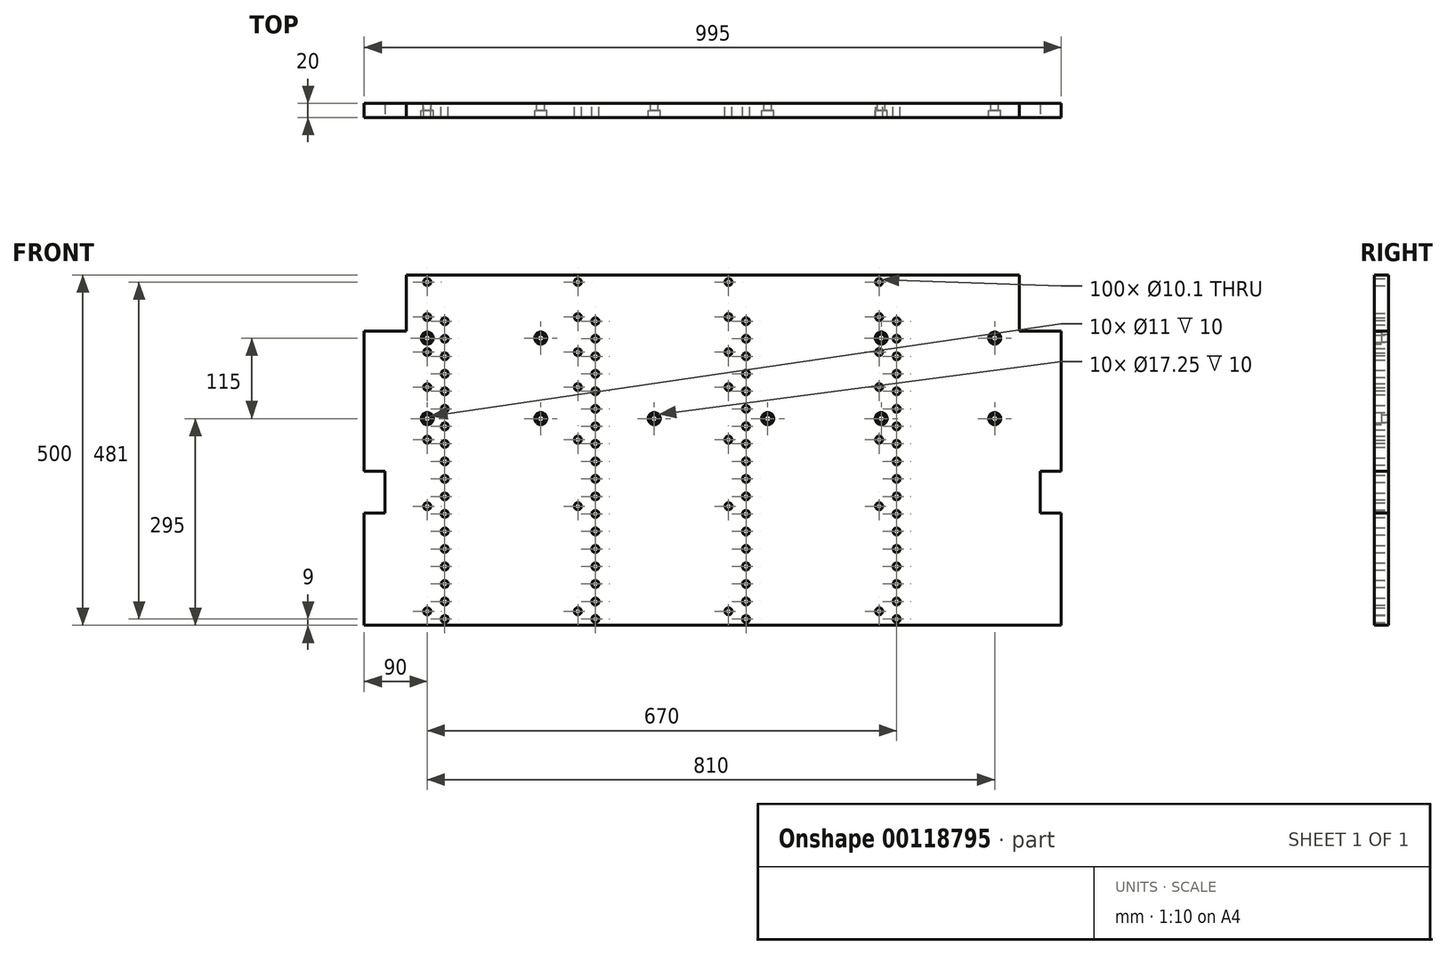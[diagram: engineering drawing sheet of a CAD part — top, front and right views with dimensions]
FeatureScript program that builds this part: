
annotation { "Feature Type Name" : "Feature", "Feature Type Description" : "" }
export const myFeature = defineFeature(function(context is Context, id is Id, definition is map)
    precondition{}
    {
        {
            var Q0;
            Q0=qCreatedBy(makeId("Front.planeOp"),FACE);
            var sketch = newSketch(context, id + "F0", { "sketchPlane" : qUnion([Q0])});
            skLineSegment(sketch, "E0.bottom", {"start": v(497.5, -250) * mm, "end": v(-497.5, -250) * mm});
            skLineSegment(sketch, "E0.top", {"start": v(437.5, 250) * mm, "end": v(-437.5, 250) * mm});
            skLineSegment(sketch, "E0.left", {"start": v(497.5, -250) * mm, "end": v(497.5, -90) * mm});
            skLineSegment(sketch, "E0.right", {"start": v(-497.5, -250) * mm, "end": v(-497.5, -90) * mm});
            skPoint(sketch, "E0.middle", {"position": v(0, 0) * mm});
            skLineSegment(sketch, "E1", {"start": v(-497.5, 170) * mm, "end": v(-437.5, 170) * mm});
            skLineSegment(sketch, "E2", {"start": v(-437.5, 170) * mm, "end": v(-437.5, 250) * mm});
            skLineSegment(sketch, "E3.MirrorCS", {"start": v(437.5, 170) * mm, "end": v(437.5, 250) * mm});
            skLineSegment(sketch, "E4.MirrorCS", {"start": v(497.5, 170) * mm, "end": v(437.5, 170) * mm});
            skLineSegment(sketch, "E5", {"start": v(-497.5, -30) * mm, "end": v(-467.5, -30) * mm});
            skLineSegment(sketch, "E6", {"start": v(-467.5, -30) * mm, "end": v(-467.5, -90) * mm});
            skLineSegment(sketch, "E7", {"start": v(-467.5, -90) * mm, "end": v(-497.5, -90) * mm});
            skLineSegment(sketch, "E8.MirrorCS", {"start": v(467.5, -30) * mm, "end": v(467.5, -90) * mm});
            skLineSegment(sketch, "E9.MirrorCS", {"start": v(467.5, -90) * mm, "end": v(497.5, -90) * mm});
            skLineSegment(sketch, "E10.MirrorCS", {"start": v(497.5, -30) * mm, "end": v(467.5, -30) * mm});
            skLineSegment(sketch, "E11.trimOffspring", {"start": v(-497.5, -30) * mm, "end": v(-497.5, 170) * mm});
            skLineSegment(sketch, "E12.trimOffspring", {"start": v(497.5, -30) * mm, "end": v(497.5, 170) * mm});
            skPoint(sketch, "E13.orphan", {"position": v(-497.5, 250) * mm});
            skPoint(sketch, "E14.orphan", {"position": v(497.5, 250) * mm});
            skSolve(sketch);
        }
        {
            var Q0;
            Q0=makeQuery(id+"F0.imprint","IMPRINT",FACE,{"disambiguationData":[TD([[makeQuery(id+"F0.imprint","IMPRINT",EDGE,{"derivedFrom":sQuery(id+"F0.wireOp",EDGE,"E0.bottom")}),-1.0]])]});
            extrude(context, id + "F1", {"entities" : qUnion([Q0]), "oppositeDirection" : true, "depth" : 20 * mm, "offsetDistance" : 25 * mm});
        }
        {
            var Q0;
            Q0=makeQuery(id+"F1.opExtrude","CAP_FACE",FACE,{"disambiguationData":[OSD([sQuery(id+"F0.wireOp",EDGE,"E0.bottom"),sQuery(id+"F0.wireOp",EDGE,"E0.top"),sQuery(id+"F0.wireOp",EDGE,"E0.left"),sQuery(id+"F0.wireOp",EDGE,"E0.right"),sQuery(id+"F0.wireOp",EDGE,"E1"),sQuery(id+"F0.wireOp",EDGE,"E2"),sQuery(id+"F0.wireOp",EDGE,"E3.MirrorCS"),sQuery(id+"F0.wireOp",EDGE,"E4.MirrorCS"),sQuery(id+"F0.wireOp",EDGE,"E5"),sQuery(id+"F0.wireOp",EDGE,"E6"),sQuery(id+"F0.wireOp",EDGE,"E7"),sQuery(id+"F0.wireOp",EDGE,"E8.MirrorCS"),sQuery(id+"F0.wireOp",EDGE,"E9.MirrorCS"),sQuery(id+"F0.wireOp",EDGE,"E10.MirrorCS"),sQuery(id+"F0.wireOp",EDGE,"E11.trimOffspring"),sQuery(id+"F0.wireOp",EDGE,"E12.trimOffspring")])],"isStart":true});
            var sketch = newSketch(context, id + "F2", { "sketchPlane" : qUnion([Q0])});
            skPoint(sketch, "E15", {"position": v(-407.5, 160) * mm});
            skPoint(sketch, "E16.0.1.0", {"position": v(-407.5, 45) * mm});
            skPoint(sketch, "E16.1.0.0", {"position": v(-245.5, 160) * mm});
            skPoint(sketch, "E16.1.1.0", {"position": v(-245.5, 45) * mm});
            skPoint(sketch, "E16.2.1.0", {"position": v(-83.5, 45) * mm});
            skPoint(sketch, "E16.3.1.0", {"position": v(78.5, 45) * mm});
            skPoint(sketch, "E16.4.0.0", {"position": v(240.5, 160) * mm});
            skPoint(sketch, "E16.4.1.0", {"position": v(240.5, 45) * mm});
            skPoint(sketch, "E16.5.0.0", {"position": v(402.5, 160) * mm});
            skPoint(sketch, "E16.5.1.0", {"position": v(402.5, 45) * mm});
            skLineSegment(sketch, "E16.direction1", {"start": v(-407.5, 160) * mm, "end": v(-245.5, 160) * mm, "construction": true});
            skLineSegment(sketch, "E16.direction2", {"start": v(-407.5, 160) * mm, "end": v(-407.5, 45) * mm, "construction": true});
            skSolve(sketch);
        }
        {
            var Q0;
            Q0=sQuery(id+"F2.wireOp",VERTEX,"E16.2.0.0");
            var Q1;
            Q1=sQuery(id+"F2.wireOp",VERTEX,"E16.2.1.0");
            var Q2;
            Q2=sQuery(id+"F2.wireOp",VERTEX,"E16.3.0.0");
            var Q3;
            Q3=sQuery(id+"F2.wireOp",VERTEX,"E15");
            var Q4;
            Q4=sQuery(id+"F2.wireOp",VERTEX,"E16.3.1.0");
            var Q5;
            Q5=sQuery(id+"F2.wireOp",VERTEX,"E16.0.1.0");
            var Q6;
            Q6=sQuery(id+"F2.wireOp",VERTEX,"E16.4.0.0");
            var Q7;
            Q7=sQuery(id+"F2.wireOp",VERTEX,"E16.1.0.0");
            var Q8;
            Q8=sQuery(id+"F2.wireOp",VERTEX,"E16.5.1.0");
            var Q9;
            Q9=sQuery(id+"F2.wireOp",VERTEX,"E16.4.1.0");
            var Q10;
            Q10=sQuery(id+"F2.wireOp",VERTEX,"E16.1.1.0");
            var Q11;
            Q11=sQuery(id+"F2.wireOp",VERTEX,"E16.5.0.0");
            var Q12;
            Q12=makeQuery(id+"F1.opExtrude","SWEPT_BODY",BODY,{"disambiguationData":[OSD([sQuery(id+"F0.wireOp",EDGE,"E0.bottom"),sQuery(id+"F0.wireOp",EDGE,"E0.top"),sQuery(id+"F0.wireOp",EDGE,"E0.left"),sQuery(id+"F0.wireOp",EDGE,"E0.right"),sQuery(id+"F0.wireOp",EDGE,"E1"),sQuery(id+"F0.wireOp",EDGE,"E2"),sQuery(id+"F0.wireOp",EDGE,"E3.MirrorCS"),sQuery(id+"F0.wireOp",EDGE,"E4.MirrorCS"),sQuery(id+"F0.wireOp",EDGE,"E5"),sQuery(id+"F0.wireOp",EDGE,"E6"),sQuery(id+"F0.wireOp",EDGE,"E7"),sQuery(id+"F0.wireOp",EDGE,"E8.MirrorCS"),sQuery(id+"F0.wireOp",EDGE,"E9.MirrorCS"),sQuery(id+"F0.wireOp",EDGE,"E10.MirrorCS"),sQuery(id+"F0.wireOp",EDGE,"E11.trimOffspring"),sQuery(id+"F0.wireOp",EDGE,"E12.trimOffspring")])]});
            hole(context, id + "F3", {"style" : HoleStyle.C_BORE, "endStyle" : HoleEndStyle.BLIND, "standardTappedOrClearance" : lookupTablePath({ "fit" : "Normal", "standard" : "ISO", "size" : "M10", "type" : "Clearance" }), "standardBlindInLast" : lookupTablePath({ "fit" : "Normal", "standard" : "ISO", "engagement" : "75%", "pitch" : "1 mm", "size" : "M10", "type" : "Clearance & tapped" }), "holeDiameter" : 11 * mm, "cBoreDiameter" : 17.25 * mm, "cBoreDepth" : 10 * mm, "majorDiameter" : 10 * mm, "holeDepth" : 35 * mm, "tappedDepth" : 32 * mm, "tapClearance" : 3, "locations" : qUnion([Q0, Q1, Q2, Q3, Q4, Q5, Q6, Q7, Q8, Q9, Q10, Q11]), "scope" : qUnion([Q12]), "startStyle" : HoleStartStyle.SKETCH});
        }
        {
            var Q0;
            Q0=makeQuery(id+"F1.opExtrude","CAP_FACE",FACE,{"disambiguationData":[OSD([sQuery(id+"F0.wireOp",EDGE,"E0.bottom"),sQuery(id+"F0.wireOp",EDGE,"E0.top"),sQuery(id+"F0.wireOp",EDGE,"E0.left"),sQuery(id+"F0.wireOp",EDGE,"E0.right"),sQuery(id+"F0.wireOp",EDGE,"E1"),sQuery(id+"F0.wireOp",EDGE,"E2"),sQuery(id+"F0.wireOp",EDGE,"E3.MirrorCS"),sQuery(id+"F0.wireOp",EDGE,"E4.MirrorCS"),sQuery(id+"F0.wireOp",EDGE,"E5"),sQuery(id+"F0.wireOp",EDGE,"E6"),sQuery(id+"F0.wireOp",EDGE,"E7"),sQuery(id+"F0.wireOp",EDGE,"E8.MirrorCS"),sQuery(id+"F0.wireOp",EDGE,"E9.MirrorCS"),sQuery(id+"F0.wireOp",EDGE,"E10.MirrorCS"),sQuery(id+"F0.wireOp",EDGE,"E11.trimOffspring"),sQuery(id+"F0.wireOp",EDGE,"E12.trimOffspring")])],"isStart":true});
            var sketch = newSketch(context, id + "F4", { "sketchPlane" : qUnion([Q0])});
            skLineSegment(sketch, "E17", {"start": v(-407.5, 250) * mm, "end": v(-407.5, -250) * mm, "construction": true});
            skPoint(sketch, "E18", {"position": v(-407.5, 240) * mm});
            skPoint(sketch, "E19", {"position": v(-407.5, 190) * mm});
            skPoint(sketch, "E20", {"position": v(-407.5, 140) * mm});
            skPoint(sketch, "E21", {"position": v(-407.5, 90) * mm});
            skPoint(sketch, "E22", {"position": v(-407.5, 15) * mm});
            skPoint(sketch, "E23", {"position": v(-407.5, -80) * mm});
            skPoint(sketch, "E24", {"position": v(-407.5, -230) * mm});
            skLineSegment(sketch, "E25.direction1", {"start": v(-407.5, -250) * mm, "end": v(-197.5, -250) * mm, "construction": true});
            skPoint(sketch, "E26.1.0.0", {"position": v(-192.5, 240) * mm});
            skPoint(sketch, "E26.1.0.1", {"position": v(-192.5, 190) * mm});
            skPoint(sketch, "E26.1.0.2", {"position": v(-192.5, 140) * mm});
            skPoint(sketch, "E26.1.0.3", {"position": v(-192.5, 90) * mm});
            skPoint(sketch, "E26.1.0.4", {"position": v(-192.5, 15) * mm});
            skPoint(sketch, "E26.1.0.5", {"position": v(-192.5, -80) * mm});
            skPoint(sketch, "E26.1.0.6", {"position": v(-192.5, -230) * mm});
            skLineSegment(sketch, "E26.1.0.7", {"start": v(-192.5, 250) * mm, "end": v(-192.5, -250) * mm, "construction": true});
            skPoint(sketch, "E26.2.0.0", {"position": v(22.5, 240) * mm});
            skPoint(sketch, "E26.2.0.1", {"position": v(22.5, 190) * mm});
            skPoint(sketch, "E26.2.0.2", {"position": v(22.5, 140) * mm});
            skPoint(sketch, "E26.2.0.3", {"position": v(22.5, 90) * mm});
            skPoint(sketch, "E26.2.0.4", {"position": v(22.5, 15) * mm});
            skPoint(sketch, "E26.2.0.5", {"position": v(22.5, -80) * mm});
            skPoint(sketch, "E26.2.0.6", {"position": v(22.5, -230) * mm});
            skLineSegment(sketch, "E26.2.0.7", {"start": v(22.5, 250) * mm, "end": v(22.5, -250) * mm, "construction": true});
            skPoint(sketch, "E26.3.0.0", {"position": v(237.5, 240) * mm});
            skPoint(sketch, "E26.3.0.1", {"position": v(237.5, 190) * mm});
            skPoint(sketch, "E26.3.0.2", {"position": v(237.5, 140) * mm});
            skPoint(sketch, "E26.3.0.3", {"position": v(237.5, 90) * mm});
            skPoint(sketch, "E26.3.0.4", {"position": v(237.5, 15) * mm});
            skPoint(sketch, "E26.3.0.5", {"position": v(237.5, -80) * mm});
            skPoint(sketch, "E26.3.0.6", {"position": v(237.5, -230) * mm});
            skLineSegment(sketch, "E26.3.0.7", {"start": v(237.5, 250) * mm, "end": v(237.5, -250) * mm, "construction": true});
            skPoint(sketch, "E26.4.0.0", {"position": v(452.5, 240) * mm});
            skPoint(sketch, "E26.4.0.1", {"position": v(452.5, 190) * mm});
            skPoint(sketch, "E26.4.0.2", {"position": v(452.5, 140) * mm});
            skPoint(sketch, "E26.4.0.3", {"position": v(452.5, 90) * mm});
            skPoint(sketch, "E26.4.0.4", {"position": v(452.5, 15) * mm});
            skPoint(sketch, "E26.4.0.5", {"position": v(452.5, -80) * mm});
            skPoint(sketch, "E26.4.0.6", {"position": v(452.5, -230) * mm});
            skLineSegment(sketch, "E26.4.0.7", {"start": v(452.5, 250) * mm, "end": v(452.5, -250) * mm, "construction": true});
            skLineSegment(sketch, "E26.direction1", {"start": v(-407.5, 190) * mm, "end": v(-192.5, 190) * mm, "construction": true});
            skSolve(sketch);
        }
        {
            var Q0;
            Q0=sQuery(id+"F4.wireOp",VERTEX,"E23");
            var Q1;
            Q1=sQuery(id+"F4.wireOp",VERTEX,"E22");
            var Q2;
            Q2=sQuery(id+"F4.wireOp",VERTEX,"E24");
            var Q3;
            Q3=sQuery(id+"F4.wireOp",VERTEX,"E21");
            var Q4;
            Q4=sQuery(id+"F4.wireOp",VERTEX,"E18");
            var Q5;
            Q5=sQuery(id+"F4.wireOp",VERTEX,"E20");
            var Q6;
            Q6=sQuery(id+"F4.wireOp",VERTEX,"E19");
            var Q7;
            Q7=sQuery(id+"F4.wireOp",VERTEX,"E26.2.0.1");
            var Q8;
            Q8=sQuery(id+"F4.wireOp",VERTEX,"E26.direction1.end");
            var Q9;
            Q9=sQuery(id+"F4.wireOp",VERTEX,"E26.3.0.3");
            var Q10;
            Q10=sQuery(id+"F4.wireOp",VERTEX,"E26.1.0.4");
            var Q11;
            Q11=sQuery(id+"F4.wireOp",VERTEX,"E26.3.0.5");
            var Q12;
            Q12=sQuery(id+"F4.wireOp",VERTEX,"E26.1.0.5");
            var Q13;
            Q13=sQuery(id+"F4.wireOp",VERTEX,"E26.1.0.6");
            var Q14;
            Q14=sQuery(id+"F4.wireOp",VERTEX,"E26.3.0.6");
            var Q15;
            Q15=sQuery(id+"F4.wireOp",VERTEX,"E26.3.0.1");
            var Q16;
            Q16=sQuery(id+"F4.wireOp",VERTEX,"E26.1.0.2");
            var Q17;
            Q17=sQuery(id+"F4.wireOp",VERTEX,"E26.2.0.5");
            var Q18;
            Q18=sQuery(id+"F4.wireOp",VERTEX,"E26.2.0.2");
            var Q19;
            Q19=sQuery(id+"F4.wireOp",VERTEX,"E26.1.0.0");
            var Q20;
            Q20=sQuery(id+"F4.wireOp",VERTEX,"E26.2.0.6");
            var Q21;
            Q21=sQuery(id+"F4.wireOp",VERTEX,"E26.1.0.3");
            var Q22;
            Q22=sQuery(id+"F4.wireOp",VERTEX,"E26.3.0.2");
            var Q23;
            Q23=sQuery(id+"F4.wireOp",VERTEX,"E26.3.0.4");
            var Q24;
            Q24=sQuery(id+"F4.wireOp",VERTEX,"E26.3.0.0");
            var Q25;
            Q25=sQuery(id+"F4.wireOp",VERTEX,"E26.2.0.0");
            var Q26;
            Q26=sQuery(id+"F4.wireOp",VERTEX,"E26.2.0.4");
            var Q27;
            Q27=sQuery(id+"F4.wireOp",VERTEX,"E26.2.0.3");
            var Q28;
            Q28=makeQuery(id+"F1.opExtrude","SWEPT_BODY",BODY,{"disambiguationData":[OSD([sQuery(id+"F0.wireOp",EDGE,"E0.bottom"),sQuery(id+"F0.wireOp",EDGE,"E0.top"),sQuery(id+"F0.wireOp",EDGE,"E0.left"),sQuery(id+"F0.wireOp",EDGE,"E0.right"),sQuery(id+"F0.wireOp",EDGE,"E1"),sQuery(id+"F0.wireOp",EDGE,"E2"),sQuery(id+"F0.wireOp",EDGE,"E3.MirrorCS"),sQuery(id+"F0.wireOp",EDGE,"E4.MirrorCS"),sQuery(id+"F0.wireOp",EDGE,"E5"),sQuery(id+"F0.wireOp",EDGE,"E6"),sQuery(id+"F0.wireOp",EDGE,"E7"),sQuery(id+"F0.wireOp",EDGE,"E8.MirrorCS"),sQuery(id+"F0.wireOp",EDGE,"E9.MirrorCS"),sQuery(id+"F0.wireOp",EDGE,"E10.MirrorCS"),sQuery(id+"F0.wireOp",EDGE,"E11.trimOffspring"),sQuery(id+"F0.wireOp",EDGE,"E12.trimOffspring")])]});
            hole(context, id + "F5", {"style" : HoleStyle.SIMPLE, "endStyle" : HoleEndStyle.THROUGH, "holeDiameter" : 10.1 * mm, "majorDiameter" : 5 * mm, "tappedDepth" : 32 * mm, "tapClearance" : 3, "locations" : qUnion([Q0, Q1, Q2, Q3, Q4, Q5, Q6, Q7, Q8, Q9, Q10, Q11, Q12, Q13, Q14, Q15, Q16, Q17, Q18, Q19, Q20, Q21, Q22, Q23, Q24, Q25, Q26, Q27]), "scope" : qUnion([Q28]), "startStyle" : HoleStartStyle.SKETCH});
        }
        {
            var Q0;
            Q0=makeQuery(id+"F1.opExtrude","CAP_FACE",FACE,{"disambiguationData":[OSD([sQuery(id+"F0.wireOp",EDGE,"E0.bottom"),sQuery(id+"F0.wireOp",EDGE,"E0.top"),sQuery(id+"F0.wireOp",EDGE,"E0.left"),sQuery(id+"F0.wireOp",EDGE,"E0.right"),sQuery(id+"F0.wireOp",EDGE,"E1"),sQuery(id+"F0.wireOp",EDGE,"E2"),sQuery(id+"F0.wireOp",EDGE,"E3.MirrorCS"),sQuery(id+"F0.wireOp",EDGE,"E4.MirrorCS"),sQuery(id+"F0.wireOp",EDGE,"E5"),sQuery(id+"F0.wireOp",EDGE,"E6"),sQuery(id+"F0.wireOp",EDGE,"E7"),sQuery(id+"F0.wireOp",EDGE,"E8.MirrorCS"),sQuery(id+"F0.wireOp",EDGE,"E9.MirrorCS"),sQuery(id+"F0.wireOp",EDGE,"E10.MirrorCS"),sQuery(id+"F0.wireOp",EDGE,"E11.trimOffspring"),sQuery(id+"F0.wireOp",EDGE,"E12.trimOffspring")])],"isStart":true});
            var sketch = newSketch(context, id + "F6", { "sketchPlane" : qUnion([Q0])});
            skPoint(sketch, "E27", {"position": v(-382.5, 184) * mm});
            skPoint(sketch, "E28.0.1.0", {"position": v(-382.5, 159) * mm});
            skPoint(sketch, "E28.0.2.0", {"position": v(-382.5, 134) * mm});
            skPoint(sketch, "E28.0.3.0", {"position": v(-382.5, 109) * mm});
            skPoint(sketch, "E28.0.4.0", {"position": v(-382.5, 84) * mm});
            skPoint(sketch, "E28.0.5.0", {"position": v(-382.5, 59) * mm});
            skPoint(sketch, "E28.0.6.0", {"position": v(-382.5, 34) * mm});
            skPoint(sketch, "E28.0.7.0", {"position": v(-382.5, 9) * mm});
            skPoint(sketch, "E28.0.8.0", {"position": v(-382.5, -16) * mm});
            skPoint(sketch, "E28.0.9.0", {"position": v(-382.5, -41) * mm});
            skPoint(sketch, "E28.0.10.0", {"position": v(-382.5, -66) * mm});
            skPoint(sketch, "E28.0.11.0", {"position": v(-382.5, -91) * mm});
            skPoint(sketch, "E28.0.12.0", {"position": v(-382.5, -116) * mm});
            skPoint(sketch, "E28.0.13.0", {"position": v(-382.5, -141) * mm});
            skPoint(sketch, "E28.0.14.0", {"position": v(-382.5, -166) * mm});
            skPoint(sketch, "E28.0.15.0", {"position": v(-382.5, -191) * mm});
            skPoint(sketch, "E28.0.16.0", {"position": v(-382.5, -216) * mm});
            skPoint(sketch, "E28.1.0.0", {"position": v(-167.5, 184) * mm});
            skPoint(sketch, "E28.1.1.0", {"position": v(-167.5, 159) * mm});
            skPoint(sketch, "E28.1.2.0", {"position": v(-167.5, 134) * mm});
            skPoint(sketch, "E28.1.3.0", {"position": v(-167.5, 109) * mm});
            skPoint(sketch, "E28.1.4.0", {"position": v(-167.5, 84) * mm});
            skPoint(sketch, "E28.1.5.0", {"position": v(-167.5, 59) * mm});
            skPoint(sketch, "E28.1.6.0", {"position": v(-167.5, 34) * mm});
            skPoint(sketch, "E28.1.7.0", {"position": v(-167.5, 9) * mm});
            skPoint(sketch, "E28.1.8.0", {"position": v(-167.5, -16) * mm});
            skPoint(sketch, "E28.1.9.0", {"position": v(-167.5, -41) * mm});
            skPoint(sketch, "E28.1.10.0", {"position": v(-167.5, -66) * mm});
            skPoint(sketch, "E28.1.11.0", {"position": v(-167.5, -91) * mm});
            skPoint(sketch, "E28.1.12.0", {"position": v(-167.5, -116) * mm});
            skPoint(sketch, "E28.1.13.0", {"position": v(-167.5, -141) * mm});
            skPoint(sketch, "E28.1.14.0", {"position": v(-167.5, -166) * mm});
            skPoint(sketch, "E28.1.15.0", {"position": v(-167.5, -191) * mm});
            skPoint(sketch, "E28.1.16.0", {"position": v(-167.5, -216) * mm});
            skPoint(sketch, "E28.2.0.0", {"position": v(47.5, 184) * mm});
            skPoint(sketch, "E28.2.1.0", {"position": v(47.5, 159) * mm});
            skPoint(sketch, "E28.2.2.0", {"position": v(47.5, 134) * mm});
            skPoint(sketch, "E28.2.3.0", {"position": v(47.5, 109) * mm});
            skPoint(sketch, "E28.2.4.0", {"position": v(47.5, 84) * mm});
            skPoint(sketch, "E28.2.5.0", {"position": v(47.5, 59) * mm});
            skPoint(sketch, "E28.2.6.0", {"position": v(47.5, 34) * mm});
            skPoint(sketch, "E28.2.7.0", {"position": v(47.5, 9) * mm});
            skPoint(sketch, "E28.2.8.0", {"position": v(47.5, -16) * mm});
            skPoint(sketch, "E28.2.9.0", {"position": v(47.5, -41) * mm});
            skPoint(sketch, "E28.2.10.0", {"position": v(47.5, -66) * mm});
            skPoint(sketch, "E28.2.11.0", {"position": v(47.5, -91) * mm});
            skPoint(sketch, "E28.2.12.0", {"position": v(47.5, -116) * mm});
            skPoint(sketch, "E28.2.13.0", {"position": v(47.5, -141) * mm});
            skPoint(sketch, "E28.2.14.0", {"position": v(47.5, -166) * mm});
            skPoint(sketch, "E28.2.15.0", {"position": v(47.5, -191) * mm});
            skPoint(sketch, "E28.2.16.0", {"position": v(47.5, -216) * mm});
            skPoint(sketch, "E28.3.0.0", {"position": v(262.5, 184) * mm});
            skPoint(sketch, "E28.3.1.0", {"position": v(262.5, 159) * mm});
            skPoint(sketch, "E28.3.2.0", {"position": v(262.5, 134) * mm});
            skPoint(sketch, "E28.3.3.0", {"position": v(262.5, 109) * mm});
            skPoint(sketch, "E28.3.4.0", {"position": v(262.5, 84) * mm});
            skPoint(sketch, "E28.3.5.0", {"position": v(262.5, 59) * mm});
            skPoint(sketch, "E28.3.6.0", {"position": v(262.5, 34) * mm});
            skPoint(sketch, "E28.3.7.0", {"position": v(262.5, 9) * mm});
            skPoint(sketch, "E28.3.8.0", {"position": v(262.5, -16) * mm});
            skPoint(sketch, "E28.3.9.0", {"position": v(262.5, -41) * mm});
            skPoint(sketch, "E28.3.10.0", {"position": v(262.5, -66) * mm});
            skPoint(sketch, "E28.3.11.0", {"position": v(262.5, -91) * mm});
            skPoint(sketch, "E28.3.12.0", {"position": v(262.5, -116) * mm});
            skPoint(sketch, "E28.3.13.0", {"position": v(262.5, -141) * mm});
            skPoint(sketch, "E28.3.14.0", {"position": v(262.5, -166) * mm});
            skPoint(sketch, "E28.3.15.0", {"position": v(262.5, -191) * mm});
            skPoint(sketch, "E28.3.16.0", {"position": v(262.5, -216) * mm});
            skLineSegment(sketch, "E28.direction1", {"start": v(-382.5, 184) * mm, "end": v(-167.5, 184) * mm, "construction": true});
            skLineSegment(sketch, "E28.direction2", {"start": v(-382.5, 184) * mm, "end": v(-382.5, 159) * mm, "construction": true});
            skLineSegment(sketch, "E29", {"start": v(-407.5, 45) * mm, "end": v(-407.5, 227.14) * mm, "construction": true});
            skPoint(sketch, "E30.0.0.17", {"position": v(-382.5, -241) * mm});
            skPoint(sketch, "E30.0.1.17", {"position": v(-167.5, -241) * mm});
            skPoint(sketch, "E30.0.2.17", {"position": v(47.5, -241) * mm});
            skPoint(sketch, "E30.0.3.17", {"position": v(262.5, -241) * mm});
            skSolve(sketch);
        }
        {
            var Q0;
            Q0=sQuery(id+"F6.wireOp",VERTEX,"E28.2.12.0");
            var Q1;
            Q1=sQuery(id+"F6.wireOp",VERTEX,"E28.3.11.0");
            var Q2;
            Q2=sQuery(id+"F6.wireOp",VERTEX,"E28.0.14.0");
            var Q3;
            Q3=sQuery(id+"F6.wireOp",VERTEX,"E28.1.13.0");
            var Q4;
            Q4=sQuery(id+"F6.wireOp",VERTEX,"E28.1.8.0");
            var Q5;
            Q5=sQuery(id+"F6.wireOp",VERTEX,"E28.2.7.0");
            var Q6;
            Q6=sQuery(id+"F6.wireOp",VERTEX,"E28.3.7.0");
            var Q7;
            Q7=sQuery(id+"F6.wireOp",VERTEX,"E28.1.9.0");
            var Q8;
            Q8=sQuery(id+"F6.wireOp",VERTEX,"E28.2.8.0");
            var Q9;
            Q9=sQuery(id+"F6.wireOp",VERTEX,"E28.1.6.0");
            var Q10;
            Q10=sQuery(id+"F6.wireOp",VERTEX,"E28.2.5.0");
            var Q11;
            Q11=sQuery(id+"F6.wireOp",VERTEX,"E28.3.5.0");
            var Q12;
            Q12=sQuery(id+"F6.wireOp",VERTEX,"E28.1.7.0");
            var Q13;
            Q13=sQuery(id+"F6.wireOp",VERTEX,"E28.2.6.0");
            var Q14;
            Q14=sQuery(id+"F6.wireOp",VERTEX,"E28.3.6.0");
            var Q15;
            Q15=sQuery(id+"F6.wireOp",VERTEX,"E28.1.4.0");
            var Q16;
            Q16=sQuery(id+"F6.wireOp",VERTEX,"E28.2.3.0");
            var Q17;
            Q17=sQuery(id+"F6.wireOp",VERTEX,"E28.3.3.0");
            var Q18;
            Q18=sQuery(id+"F6.wireOp",VERTEX,"E28.1.5.0");
            var Q19;
            Q19=sQuery(id+"F6.wireOp",VERTEX,"E28.2.4.0");
            var Q20;
            Q20=sQuery(id+"F6.wireOp",VERTEX,"E28.3.4.0");
            var Q21;
            Q21=sQuery(id+"F6.wireOp",VERTEX,"E28.3.1.0");
            var Q22;
            Q22=sQuery(id+"F6.wireOp",VERTEX,"E28.0.5.0");
            var Q23;
            Q23=sQuery(id+"F6.wireOp",VERTEX,"E28.1.3.0");
            var Q24;
            Q24=sQuery(id+"F6.wireOp",VERTEX,"E28.2.2.0");
            var Q25;
            Q25=sQuery(id+"F6.wireOp",VERTEX,"E28.3.2.0");
            var Q26;
            Q26=sQuery(id+"F6.wireOp",VERTEX,"E28.0.4.0");
            var Q27;
            Q27=sQuery(id+"F6.wireOp",VERTEX,"E28.0.7.0");
            var Q28;
            Q28=sQuery(id+"F6.wireOp",VERTEX,"E28.0.6.0");
            var Q29;
            Q29=sQuery(id+"F6.wireOp",VERTEX,"E28.0.9.0");
            var Q30;
            Q30=sQuery(id+"F6.wireOp",VERTEX,"E28.0.8.0");
            var Q31;
            Q31=sQuery(id+"F6.wireOp",VERTEX,"E28.0.10.0");
            var Q32;
            Q32=sQuery(id+"F6.wireOp",VERTEX,"E28.0.1.0");
            var Q33;
            Q33=sQuery(id+"F6.wireOp",VERTEX,"E27");
            var Q34;
            Q34=sQuery(id+"F6.wireOp",VERTEX,"E28.0.3.0");
            var Q35;
            Q35=sQuery(id+"F6.wireOp",VERTEX,"E28.0.2.0");
            var Q36;
            Q36=sQuery(id+"F6.wireOp",VERTEX,"E28.2.10.0");
            var Q37;
            Q37=sQuery(id+"F6.wireOp",VERTEX,"E28.0.13.0");
            var Q38;
            Q38=sQuery(id+"F6.wireOp",VERTEX,"E28.3.0.0");
            var Q39;
            Q39=sQuery(id+"F6.wireOp",VERTEX,"E28.3.9.0");
            var Q40;
            Q40=sQuery(id+"F6.wireOp",VERTEX,"E28.3.16.0");
            var Q41;
            Q41=sQuery(id+"F6.wireOp",VERTEX,"E28.1.2.0");
            var Q42;
            Q42=sQuery(id+"F6.wireOp",VERTEX,"E28.1.11.0");
            var Q43;
            Q43=sQuery(id+"F6.wireOp",VERTEX,"E28.2.1.0");
            var Q44;
            Q44=sQuery(id+"F6.wireOp",VERTEX,"E28.2.11.0");
            var Q45;
            Q45=sQuery(id+"F6.wireOp",VERTEX,"E28.0.12.0");
            var Q46;
            Q46=sQuery(id+"F6.wireOp",VERTEX,"E28.2.15.0");
            var Q47;
            Q47=sQuery(id+"F6.wireOp",VERTEX,"E28.3.10.0");
            var Q48;
            Q48=sQuery(id+"F6.wireOp",VERTEX,"E28.3.14.0");
            var Q49;
            Q49=sQuery(id+"F6.wireOp",VERTEX,"E28.1.0.0");
            var Q50;
            Q50=sQuery(id+"F6.wireOp",VERTEX,"E28.1.12.0");
            var Q51;
            Q51=sQuery(id+"F6.wireOp",VERTEX,"E28.1.16.0");
            var Q52;
            Q52=sQuery(id+"F6.wireOp",VERTEX,"E28.2.9.0");
            var Q53;
            Q53=sQuery(id+"F6.wireOp",VERTEX,"E28.0.11.0");
            var Q54;
            Q54=sQuery(id+"F6.wireOp",VERTEX,"E28.2.16.0");
            var Q55;
            Q55=sQuery(id+"F6.wireOp",VERTEX,"E28.3.15.0");
            var Q56;
            Q56=sQuery(id+"F6.wireOp",VERTEX,"E28.3.8.0");
            var Q57;
            Q57=sQuery(id+"F6.wireOp",VERTEX,"E28.1.1.0");
            var Q58;
            Q58=sQuery(id+"F6.wireOp",VERTEX,"E28.1.10.0");
            var Q59;
            Q59=sQuery(id+"F6.wireOp",VERTEX,"E28.2.0.0");
            var Q60;
            Q60=sQuery(id+"F6.wireOp",VERTEX,"E28.2.13.0");
            var Q61;
            Q61=sQuery(id+"F6.wireOp",VERTEX,"E28.3.12.0");
            var Q62;
            Q62=sQuery(id+"F6.wireOp",VERTEX,"E28.0.15.0");
            var Q63;
            Q63=sQuery(id+"F6.wireOp",VERTEX,"E28.1.14.0");
            var Q64;
            Q64=sQuery(id+"F6.wireOp",VERTEX,"E28.2.14.0");
            var Q65;
            Q65=sQuery(id+"F6.wireOp",VERTEX,"E28.3.13.0");
            var Q66;
            Q66=sQuery(id+"F6.wireOp",VERTEX,"E28.0.16.0");
            var Q67;
            Q67=sQuery(id+"F6.wireOp",VERTEX,"E28.1.15.0");
            var Q68;
            Q68=sQuery(id+"F6.wireOp",VERTEX,"E30.0.0.17");
            var Q69;
            Q69=sQuery(id+"F6.wireOp",VERTEX,"E30.0.1.17");
            var Q70;
            Q70=sQuery(id+"F6.wireOp",VERTEX,"E30.0.2.17");
            var Q71;
            Q71=sQuery(id+"F6.wireOp",VERTEX,"E30.0.3.17");
            var Q72;
            Q72=makeQuery(id+"F1.opExtrude","SWEPT_BODY",BODY,{"disambiguationData":[OSD([sQuery(id+"F0.wireOp",EDGE,"E0.bottom"),sQuery(id+"F0.wireOp",EDGE,"E0.top"),sQuery(id+"F0.wireOp",EDGE,"E0.left"),sQuery(id+"F0.wireOp",EDGE,"E0.right"),sQuery(id+"F0.wireOp",EDGE,"E1"),sQuery(id+"F0.wireOp",EDGE,"E2"),sQuery(id+"F0.wireOp",EDGE,"E3.MirrorCS"),sQuery(id+"F0.wireOp",EDGE,"E4.MirrorCS"),sQuery(id+"F0.wireOp",EDGE,"E5"),sQuery(id+"F0.wireOp",EDGE,"E6"),sQuery(id+"F0.wireOp",EDGE,"E7"),sQuery(id+"F0.wireOp",EDGE,"E8.MirrorCS"),sQuery(id+"F0.wireOp",EDGE,"E9.MirrorCS"),sQuery(id+"F0.wireOp",EDGE,"E10.MirrorCS"),sQuery(id+"F0.wireOp",EDGE,"E11.trimOffspring"),sQuery(id+"F0.wireOp",EDGE,"E12.trimOffspring")])]});
            hole(context, id + "F7", {"style" : HoleStyle.SIMPLE, "endStyle" : HoleEndStyle.THROUGH, "holeDiameter" : 10.1 * mm, "majorDiameter" : 5 * mm, "tappedDepth" : 32 * mm, "tapClearance" : 3, "locations" : qUnion([Q0, Q1, Q2, Q3, Q4, Q5, Q6, Q7, Q8, Q9, Q10, Q11, Q12, Q13, Q14, Q15, Q16, Q17, Q18, Q19, Q20, Q21, Q22, Q23, Q24, Q25, Q26, Q27, Q28, Q29, Q30, Q31, Q32, Q33, Q34, Q35, Q36, Q37, Q38, Q39, Q40, Q41, Q42, Q43, Q44, Q45, Q46, Q47, Q48, Q49, Q50, Q51, Q52, Q53, Q54, Q55, Q56, Q57, Q58, Q59, Q60, Q61, Q62, Q63, Q64, Q65, Q66, Q67, Q68, Q69, Q70, Q71]), "scope" : qUnion([Q72]), "startStyle" : HoleStartStyle.SKETCH});
        }
    });
